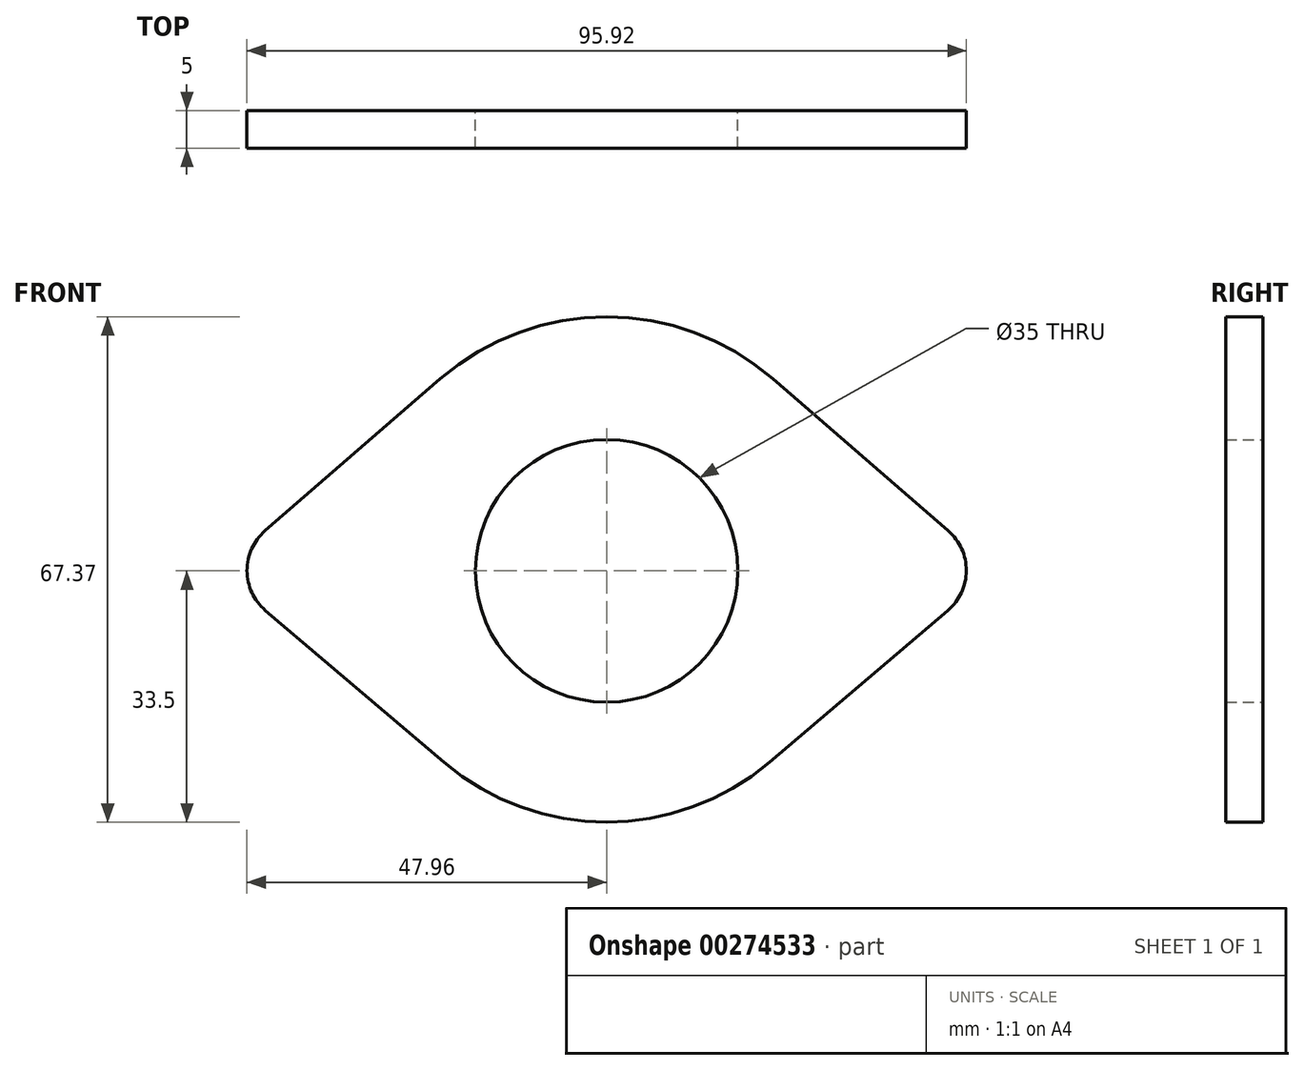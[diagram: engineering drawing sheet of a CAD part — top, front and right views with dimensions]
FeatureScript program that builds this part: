
annotation { "Feature Type Name" : "Feature", "Feature Type Description" : "" }
export const myFeature = defineFeature(function(context is Context, id is Id, definition is map)
    precondition{}
    {
        {
            var Q0;
            Q0=qCreatedBy(makeId("Front.planeOp"),FACE);
            var sketch = newSketch(context, id + "F0", { "sketchPlane" : qUnion([Q0])});
            skLineSegment(sketch, "E0", {"start": v(-45.55, 5.34) * mm, "end": v(-22.18, 25.6) * mm});
            skLineSegment(sketch, "E1", {"start": v(22.18, 25.6) * mm, "end": v(45.55, 5.34) * mm});
            skLineSegment(sketch, "E2", {"start": v(45.5, -5.28) * mm, "end": v(21.7, -25.52) * mm});
            skLineSegment(sketch, "E3", {"start": v(-21.7, -25.52) * mm, "end": v(-45.5, -5.28) * mm});
            skPoint(sketch, "E4.visualSharp", {"position": v(0, 44.82) * mm});
            skArc(sketch, "E4.filletArc", {"start": v(22.18, 25.6) * mm, "mid": v(0, 33.87) * mm, "end": v(-22.18, 25.6) * mm});
            skPoint(sketch, "E5.visualSharp", {"position": v(0, -43.98) * mm});
            skArc(sketch, "E5.filletArc", {"start": v(-21.7, -25.52) * mm, "mid": v(0, -33.5) * mm, "end": v(21.7, -25.52) * mm});
            skPoint(sketch, "E6.visualSharp", {"position": v(-51.71, 0) * mm});
            skArc(sketch, "E6.filletArc", {"start": v(-45.55, 5.34) * mm, "mid": v(-47.96, 0.02) * mm, "end": v(-45.5, -5.28) * mm});
            skPoint(sketch, "E7.visualSharp", {"position": v(51.71, 0) * mm});
            skArc(sketch, "E7.filletArc", {"start": v(45.5, -5.28) * mm, "mid": v(47.96, 0.02) * mm, "end": v(45.55, 5.34) * mm});
            skSolve(sketch);
        }
        {
            var Q0;
            Q0=makeQuery(id+"F0.imprint","IMPRINT",FACE,{"disambiguationData":[TD([[makeQuery(id+"F0.imprint","IMPRINT",EDGE,{"derivedFrom":sQuery(id+"F0.wireOp",EDGE,"E0")}),-1.0]])]});
            extrude(context, id + "F1", {"entities" : qUnion([Q0]), "depth" : 5 * mm});
        }
        {
            var Q0;
            Q0=makeQuery(id+"F1.opExtrude","CAP_FACE",FACE,{"disambiguationData":[OSD([sQuery(id+"F0.wireOp",EDGE,"E0"),sQuery(id+"F0.wireOp",EDGE,"E1"),sQuery(id+"F0.wireOp",EDGE,"E2"),sQuery(id+"F0.wireOp",EDGE,"E3"),sQuery(id+"F0.wireOp",EDGE,"E4.filletArc"),sQuery(id+"F0.wireOp",EDGE,"E5.filletArc"),sQuery(id+"F0.wireOp",EDGE,"E6.filletArc"),sQuery(id+"F0.wireOp",EDGE,"E7.filletArc")])],"isStart":false});
            var sketch = newSketch(context, id + "F2", { "sketchPlane" : qUnion([Q0])});
            skPoint(sketch, "E8", {"position": v(0, 0) * mm});
            skPoint(sketch, "E9", {"position": v(38.3, 0) * mm});
            skPoint(sketch, "E10", {"position": v(-40.96, 0.05) * mm});
            skSolve(sketch);
        }
        {
            var Q0;
            Q0=sQuery(id+"F2.wireOp",VERTEX,"E8");
            var Q1;
            Q1=makeQuery(id+"F1.opExtrude","SWEPT_BODY",BODY,{"disambiguationData":[OSD([sQuery(id+"F0.wireOp",EDGE,"E0"),sQuery(id+"F0.wireOp",EDGE,"E1"),sQuery(id+"F0.wireOp",EDGE,"E2"),sQuery(id+"F0.wireOp",EDGE,"E3"),sQuery(id+"F0.wireOp",EDGE,"E4.filletArc"),sQuery(id+"F0.wireOp",EDGE,"E5.filletArc"),sQuery(id+"F0.wireOp",EDGE,"E6.filletArc"),sQuery(id+"F0.wireOp",EDGE,"E7.filletArc")])]});
            hole(context, id + "F3", {"style" : HoleStyle.SIMPLE, "endStyle" : HoleEndStyle.THROUGH, "holeDiameter" : 35 * mm, "tappedDepth" : 12 * mm, "tapClearance" : 3, "startFromSketch" : true, "locations" : qUnion([Q0]), "scope" : qUnion([Q1])});
        }
    });
